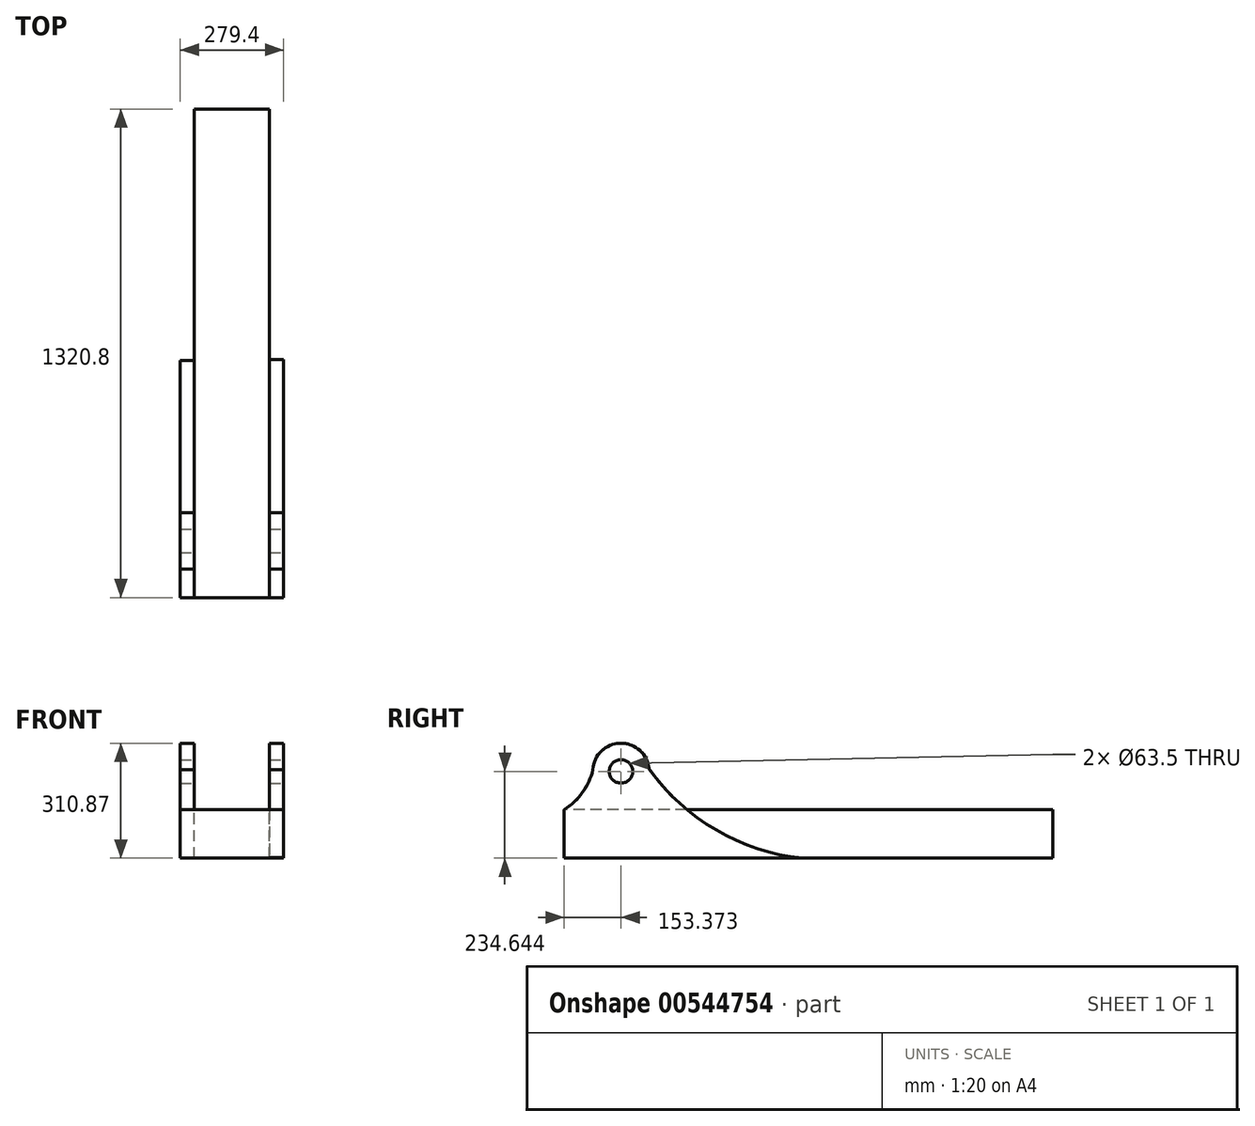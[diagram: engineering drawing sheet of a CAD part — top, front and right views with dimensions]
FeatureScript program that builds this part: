
annotation { "Feature Type Name" : "Feature", "Feature Type Description" : "" }
export const myFeature = defineFeature(function(context is Context, id is Id, definition is map)
    precondition{}
    {
        {
            var Q0;
            Q0=qCreatedBy(makeId("Right.planeOp"),FACE);
            var sketch = newSketch(context, id + "F0", { "sketchPlane" : qUnion([Q0])});
            skLineSegment(sketch, "E0", {"start": v(-939.88, 143.73) * mm, "end": v(380.92, 143.73) * mm});
            skLineSegment(sketch, "E1", {"start": v(380.92, 143.73) * mm, "end": v(380.92, 275.59) * mm});
            skLineSegment(sketch, "E2", {"start": v(380.92, 275.59) * mm, "end": v(-939.88, 275.59) * mm});
            skLineSegment(sketch, "E3", {"start": v(-939.88, 275.59) * mm, "end": v(-939.88, 143.73) * mm});
            skCircle(sketch, "E4", {"center": v(-773.36, 382.8) * mm, "radius": 76.2 * mm});
            skArc(sketch, "E5", {"start": v(-939.88, 275.59) * mm, "mid": v(-883.94, 326.33) * mm, "end": v(-848.85, 393.21) * mm});
            skArc(sketch, "E6", {"start": v(-698.74, 398.2) * mm, "mid": v(-562.27, 242.32) * mm, "end": v(-380.06, 143.73) * mm});
            skPoint(sketch, "E7", {"position": v(-939.88, 275.59) * mm});
            skPoint(sketch, "E8", {"position": v(-773.36, 275.59) * mm});
            skPoint(sketch, "E9", {"position": v(-600.43, 275.59) * mm});
            skPoint(sketch, "E10", {"position": v(-380.06, 143.73) * mm});
            skPoint(sketch, "E11", {"position": v(-698.74, 398.2) * mm});
            skPoint(sketch, "E12", {"position": v(-848.85, 393.21) * mm});
            skSolve(sketch);
        }
        {
            var Q0;
            {var subQ0=sQuery(id+"F0.wireOp",EDGE,"E1");Q0=makeQuery(id+"F0.imprint","IMPRINT",FACE,{"disambiguationData":[TD([[makeQuery(id+"F0.imprint","IMPRINT",EDGE,{"derivedFrom":subQ0}),1.0]])]});}
            var Q1;
            {var subQ0=sQuery(id+"F0.wireOp",EDGE,"E3");Q1=makeQuery(id+"F0.imprint","IMPRINT",FACE,{"disambiguationData":[TD([[makeQuery(id+"F0.imprint","IMPRINT",EDGE,{"derivedFrom":subQ0}),1.0]])]});}
            extrude(context, id + "F1", {"entities" : qUnion([Q0, Q1]), "depth" : 203.2 * mm, "offsetDistance" : 25.4 * mm});
        }
        {
            var Q0;
            Q0=makeQuery(id+"F1.opExtrude","CAP_FACE",FACE,{"disambiguationData":[OSD([sQuery(id+"F0.wireOp",EDGE,"E0"),sQuery(id+"F0.wireOp",EDGE,"E1"),sQuery(id+"F0.wireOp",EDGE,"E2"),sQuery(id+"F0.wireOp",EDGE,"E3")])],"isStart":false});
            var sketch = newSketch(context, id + "F2", { "sketchPlane" : qUnion([Q0])});
            skSolve(sketch);
        }
        {
            var Q0;
            Q0=makeQuery(id+"F2.imprint","IMPRINT",FACE,{"disambiguationData":[TD([[makeQuery(id+"F2.imprint","IMPRINT",EDGE,{"derivedFrom":makeQuery(id+"F1.opExtrude","CAP_EDGE",EDGE,{"disambiguationData":[OSD([sQuery(id+"F0.wireOp",EDGE,"E0")])],"isStart":false})}),1.0]])]});
            var sketch = newSketch(context, id + "F3", { "sketchPlane" : qUnion([Q0])});
            skCircle(sketch, "E13", {"center": v(-786.5, 378.37) * mm, "radius": 76.2 * mm});
            skArc(sketch, "E14", {"start": v(-939.87, 275.59) * mm, "mid": v(-890.43, 321.45) * mm, "end": v(-862.57, 382.86) * mm});
            skArc(sketch, "E15", {"start": v(-710.56, 384.58) * mm, "mid": v(-529.42, 220.06) * mm, "end": v(-296.9, 143.84) * mm});
            skLineSegment(sketch, "E16", {"start": v(-939.87, 275.59) * mm, "end": v(-939.87, 146.1) * mm});
            skLineSegment(sketch, "E17", {"start": v(-939.87, 146.1) * mm, "end": v(-296.9, 143.84) * mm});
            skSolve(sketch);
        }
        {
            var Q0;
            Q0=makeQuery(id+"F1.opExtrude","CAP_FACE",FACE,{"disambiguationData":[OSD([sQuery(id+"F0.wireOp",EDGE,"E0"),sQuery(id+"F0.wireOp",EDGE,"E1"),sQuery(id+"F0.wireOp",EDGE,"E2"),sQuery(id+"F0.wireOp",EDGE,"E3")])],"isStart":true});
            var sketch = newSketch(context, id + "F4", { "sketchPlane" : qUnion([Q0])});
            skCircle(sketch, "E18", {"center": v(786.49, 378.4) * mm, "radius": 76.2 * mm});
            skArc(sketch, "E19", {"start": v(862.54, 383.06) * mm, "mid": v(890.22, 321.41) * mm, "end": v(939.88, 275.59) * mm});
            skArc(sketch, "E20", {"start": v(299.4, 143.73) * mm, "mid": v(531.04, 220.44) * mm, "end": v(710.63, 385.65) * mm});
            skLineSegment(sketch, "E21", {"start": v(299.4, 143.73) * mm, "end": v(939.88, 143.73) * mm});
            skLineSegment(sketch, "E22", {"start": v(939.88, 143.73) * mm, "end": v(939.88, 275.59) * mm});
            skSolve(sketch);
        }
        {
            var Q0;
            {var subQ0=sQuery(id+"F4.wireOp",EDGE,"E21");Q0=makeQuery(id+"F4.imprint","IMPRINT",FACE,{"disambiguationData":[TD([[makeQuery(id+"F4.imprint","IMPRINT",EDGE,{"derivedFrom":subQ0}),-1.0]])]});}
            var Q1;
            {var subQ0=sQuery(id+"F4.wireOp",EDGE,"E19");Q1=makeQuery(id+"F4.imprint","IMPRINT",FACE,{"disambiguationData":[TD([[makeQuery(id+"F4.imprint","IMPRINT",EDGE,{"derivedFrom":subQ0}),-1.0]])]});}
            var Q2;
            {var subQ0=sQuery(id+"F4.wireOp",EDGE,"E18");var subQ1=makeQuery(id+"F4.imprint","INTERSECT",VERTEX,{"derivedFrom":[subQ0,sQuery(id+"F4.wireOp",EDGE,"E19")]});Q2=makeQuery(id+"F4.imprint","IMPRINT",FACE,{"disambiguationData":[TD([[makeQuery(id+"F4.imprint","IMPRINT",EDGE,{"disambiguationData":[TD([[subQ1,-1.0]])],"derivedFrom":subQ0}),1.0]])]});}
            extrude(context, id + "F5", {"entities" : qUnion([Q0, Q1, Q2]), "operationType" : NewBodyOperationType.ADD, "depth" : 38.1 * mm, "offsetDistance" : 25.4 * mm});
        }
        {
            var Q0;
            Q0 = qSketchRegion(id + "F3", true);
            extrude(context, id + "F6", {"entities" : qUnion([Q0]), "operationType" : NewBodyOperationType.ADD, "depth" : 38.1 * mm, "offsetDistance" : 25.4 * mm});
        }
        {
            var Q0;
            Q0=makeQuery(id+"F6.opExtrude","CAP_FACE",FACE,{"disambiguationData":[OSD([sQuery(id+"F3.wireOp",EDGE,"E13"),sQuery(id+"F3.wireOp",EDGE,"E14"),sQuery(id+"F3.wireOp",EDGE,"E15"),sQuery(id+"F3.wireOp",EDGE,"E16"),sQuery(id+"F3.wireOp",EDGE,"E17")])],"isStart":false});
            var sketch = newSketch(context, id + "F7", { "sketchPlane" : qUnion([Q0])});
            skPoint(sketch, "E23", {"position": v(-786.5, 378.37) * mm});
            skSolve(sketch);
        }
        {
            var Q0;
            Q0=sQuery(id+"F7.wireOp",VERTEX,"E23");
            var Q1;
            Q1=makeQuery(id+"F1.opExtrude","SWEPT_BODY",BODY,{"disambiguationData":[OSD([sQuery(id+"F0.wireOp",EDGE,"E0"),sQuery(id+"F0.wireOp",EDGE,"E1"),sQuery(id+"F0.wireOp",EDGE,"E2"),sQuery(id+"F0.wireOp",EDGE,"E3")])]});
            hole(context, id + "F8", {"style" : HoleStyle.SIMPLE, "endStyle" : HoleEndStyle.THROUGH, "holeDiameter" : 63.5 * mm, "isTappedThrough" : true, "tappedDepth" : 12.7 * mm, "tapClearance" : 3, "locations" : qUnion([Q0]), "scope" : qUnion([Q1])});
        }
        {
            var Q0;
            Q0=makeQuery(id+"F1.opExtrude","SWEPT_FACE",FACE,{"disambiguationData":[OSD([sQuery(id+"F0.wireOp",EDGE,"E1")])]});
            var sketch = newSketch(context, id + "F9", { "sketchPlane" : qUnion([Q0])});
            skLineSegment(sketch, "E24", {"start": v(-193.68, 266.05) * mm, "end": v(-193.68, 153.25) * mm});
            skLineSegment(sketch, "E25", {"start": v(-193.68, 153.25) * mm, "end": v(-9.52, 153.25) * mm});
            skLineSegment(sketch, "E26", {"start": v(-9.52, 153.25) * mm, "end": v(-9.53, 267.25) * mm});
            skLineSegment(sketch, "E27", {"start": v(-9.53, 267.25) * mm, "end": v(-193.68, 266.05) * mm});
            skSolve(sketch);
        }
        {
            var Q0;
            Q0=makeQuery(id+"F9.imprint","IMPRINT",FACE,{"disambiguationData":[TD([[makeQuery(id+"F9.imprint","IMPRINT",EDGE,{"derivedFrom":sQuery(id+"F9.wireOp",EDGE,"E24")}),1.0]])]});
            extrude(context, id + "F10", {"entities" : qUnion([Q0]), "operationType" : NewBodyOperationType.ADD, "oppositeDirection" : true, "depth" : 1265.9 * mm, "offsetDistance" : 25.4 * mm});
        }
    });
